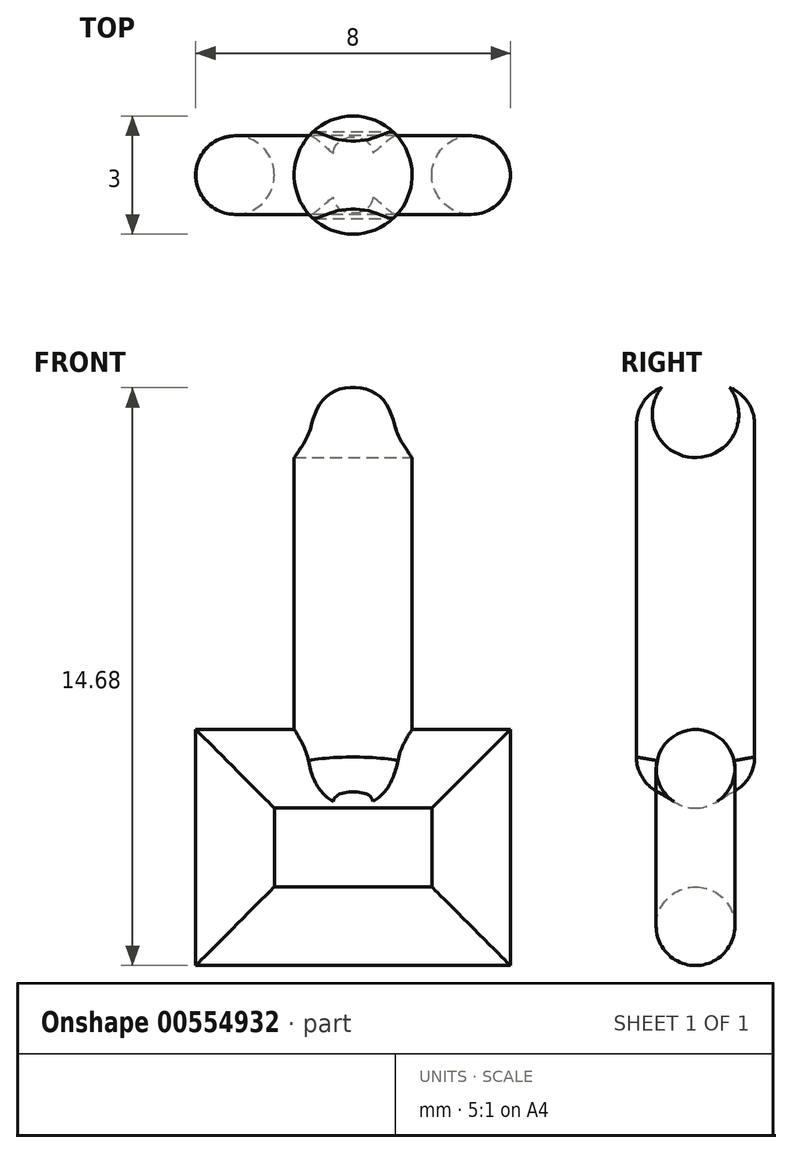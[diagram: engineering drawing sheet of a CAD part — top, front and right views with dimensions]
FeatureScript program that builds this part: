
annotation { "Feature Type Name" : "Feature", "Feature Type Description" : "" }
export const myFeature = defineFeature(function(context is Context, id is Id, definition is map)
    precondition{}
    {
        {
            var Q0;
            Q0=qCreatedBy(makeId("Front.planeOp"),FACE);
            var sketch = newSketch(context, id + "F0", { "sketchPlane" : qUnion([Q0])});
            skLineSegment(sketch, "E0.bottom", {"start": v(3, 4) * mm, "end": v(-3, 4) * mm});
            skLineSegment(sketch, "E0.top", {"start": v(3, 0) * mm, "end": v(-3, 0) * mm});
            skLineSegment(sketch, "E0.left", {"start": v(3, 4) * mm, "end": v(3, 0) * mm});
            skLineSegment(sketch, "E0.right", {"start": v(-3, 4) * mm, "end": v(-3, 0) * mm});
            skSolve(sketch);
        }
        {
            var Q0;
            Q0=qCreatedBy(makeId("Right.planeOp"),FACE);
            var sketch = newSketch(context, id + "F1", { "sketchPlane" : qUnion([Q0])});
            skPoint(sketch, "E1.0", {"position": v(0, 4) * mm});
            skPoint(sketch, "E2.0", {"position": v(0, 0) * mm});
            skPoint(sketch, "E3.0", {"position": v(0, 2) * mm});
            skCircle(sketch, "E4", {"center": v(0, 4) * mm, "radius": 1 * mm});
            skSolve(sketch);
        }
        {
            var Q0;
            Q0=makeQuery(id+"F1.imprint","IMPRINT",FACE,{"disambiguationData":[TD([[makeQuery(id+"F1.imprint","IMPRINT",EDGE,{"derivedFrom":sQuery(id+"F1.wireOp",EDGE,"E4")}),1.0]])]});
            var Q1;
            Q1=sQuery(id+"F0.wireOp",EDGE,"E0.bottom");
            var Q2;
            Q2=sQuery(id+"F0.wireOp",EDGE,"E0.left");
            var Q3;
            Q3=sQuery(id+"F0.wireOp",EDGE,"E0.right");
            var Q4;
            Q4=sQuery(id+"F0.wireOp",EDGE,"E0.top");
            sweep(context, id + "F2", {"profiles" : qUnion([Q0]), "path" : qUnion([Q1, Q2, Q3, Q4])});
        }
        {
            var Q0;
            Q0=qCreatedBy(makeId("Top.planeOp"),FACE);
            cPlane(context, id + "F3", {"entities" : qUnion([Q0]), "cplaneType" : CPlaneType.OFFSET, "offset" : 5 * mm, "width" : 150 * mm, "height" : 150 * mm});
        }
        {
            var Q0;
            Q0=qCreatedBy(id+"F3.planeOp",FACE);
            var sketch = newSketch(context, id + "F4", { "sketchPlane" : qUnion([Q0])});
            skCircle(sketch, "E5", {"center": v(0, 0) * mm, "radius": 1.5 * mm});
            skSolve(sketch);
        }
        {
            var Q0;
            Q0 = qSketchRegion(id + "F4", true);
            extrude(context, id + "F5", {"entities" : qUnion([Q0]), "operationType" : NewBodyOperationType.ADD, "oppositeDirection" : true, "depth" : 1 * mm, "offsetDistance" : 25 * mm});
        }
        {
            var Q0;
            Q0 = qSketchRegion(id + "F4", true);
            extrude(context, id + "F6", {"entities" : qUnion([Q0]), "operationType" : NewBodyOperationType.ADD, "depth" : 8 * mm, "offsetDistance" : 25 * mm});
        }
        {
            var Q0;
            Q0=qCreatedBy(makeId("Right.planeOp"),FACE);
            var sketch = newSketch(context, id + "F7", { "sketchPlane" : qUnion([Q0])});
            skLineSegment(sketch, "E6.0", {"start": v(-1.5, 13) * mm, "end": v(1.5, 13) * mm});
            skArc(sketch, "E7", {"start": v(-1.5, 13) * mm, "mid": v(0, 14.5) * mm, "end": v(1.5, 13) * mm});
            skLineSegment(sketch, "E8", {"start": v(0, 13) * mm, "end": v(0, 14.5) * mm});
            skSolve(sketch);
        }
        {
            var Q0;
            {var subQ3=sQuery(id+"F7.wireOp",EDGE,"E8");Q0=makeQuery(id+"F7.imprint","IMPRINT",FACE,{"disambiguationData":[TD([[makeQuery(id+"F7.imprint","IMPRINT",EDGE,{"derivedFrom":subQ3}),1.0]])]});}
            var Q1;
            Q1=sQuery(id+"F7.wireOp",EDGE,"E8");
            revolve(context, id + "F8", {"operationType" : NewBodyOperationType.ADD, "entities" : qUnion([Q0]), "axis" : qUnion([Q1]), "revolveType" : RevolveType.FULL});
        }
        {
            var Q0;
            Q0=qCreatedBy(makeId("Right.planeOp"),FACE);
            var sketch = newSketch(context, id + "F9", { "sketchPlane" : qUnion([Q0])});
            skArc(sketch, "E9", {"start": v(1.3, 13.75) * mm, "mid": v(0, 14.5) * mm, "end": v(-1.3, 13.75) * mm});
            skLineSegment(sketch, "E10.0", {"start": v(-1.1, 13) * mm, "end": v(1.1, 13) * mm});
            skCircle(sketch, "E11", {"center": v(0, 13) * mm, "radius": 1.1 * mm});
            skLineSegment(sketch, "E12", {"start": v(-1.3, 13.75) * mm, "end": v(1.3, 13.75) * mm});
            skPoint(sketch, "E13.orphan", {"position": v(1.5, 13) * mm});
            skPoint(sketch, "E14.orphan", {"position": v(-1.5, 13) * mm});
            skSolve(sketch);
        }
        {
            var Q0;
            Q0 = qSketchRegion(id + "F9", true);
            extrude(context, id + "F10", {"entities" : qUnion([Q0]), "operationType" : NewBodyOperationType.REMOVE, "endBound" : BoundingType.SYMMETRIC, "oppositeDirection" : true, "depth" : 25 * mm, "offsetDistance" : 25 * mm});
        }
        {
            var Q0;
            {var subQ0=sQuery(id+"F9.wireOp",EDGE,"E12");Q0=makeQuery(id+"F10.boolean.opBoolean","INTERSECT",EDGE,{"derivedFrom":[makeQuery(id+"F8.opRevolve","SWEPT_FACE",FACE,{"disambiguationData":[OSD([sQuery(id+"F7.wireOp",EDGE,"E7")])]}),makeQuery(id+"F10.opExtrude","SWEPT_FACE",FACE,{"disambiguationData":[OSD([subQ0]),TDD([makeQuery(id+"F9.imprint","IMPRINT",EDGE,{"disambiguationData":[TD([[makeQuery(id+"F9.imprint","INTERSECT",VERTEX,{"disambiguationData":[OD(1.0)],"derivedFrom":[sQuery(id+"F9.wireOp",EDGE,"E9"),subQ0]}),-1.0]])],"derivedFrom":subQ0})])]})]});}
            var Q1;
            {var subQ0=sQuery(id+"F9.wireOp",EDGE,"E12");Q1=makeQuery(id+"F10.boolean.opBoolean","INTERSECT",EDGE,{"derivedFrom":[makeQuery(id+"F8.opRevolve","SWEPT_FACE",FACE,{"disambiguationData":[OSD([sQuery(id+"F7.wireOp",EDGE,"E7")])]}),makeQuery(id+"F10.opExtrude","SWEPT_FACE",FACE,{"disambiguationData":[OSD([subQ0]),TDD([makeQuery(id+"F9.imprint","IMPRINT",EDGE,{"disambiguationData":[TD([[makeQuery(id+"F9.imprint","INTERSECT",VERTEX,{"disambiguationData":[OD(0.0)],"derivedFrom":[sQuery(id+"F9.wireOp",EDGE,"E9"),subQ0]}),1.0]])],"derivedFrom":subQ0})])]})]});}
            fillet(context, id + "F11", {"entities" : qUnion([Q0, Q1]), "radius" : 1 * mm, "tangentPropagation" : true, "allowEdgeOverflow" : false});
        }
        {
            var Q0;
            Q0=makeQuery(id+"F5.boolean.opBoolean","INTERSECT",EDGE,{"disambiguationData":[OD(0.0)],"derivedFrom":[makeQuery(id+"F2.opSweep","SWEPT_FACE",FACE,{"disambiguationData":[OSD([sQuery(id+"F0.wireOp",EDGE,"E0.bottom"),sQuery(id+"F1.wireOp",EDGE,"E4")])]}),makeQuery(id+"F5.opExtrude","CAP_FACE",FACE,{"disambiguationData":[OSD([sQuery(id+"F4.wireOp",EDGE,"E5")])],"isStart":false})]});
            var Q1;
            Q1=makeQuery(id+"F5.boolean.opBoolean","INTERSECT",EDGE,{"disambiguationData":[OD(1.0)],"derivedFrom":[makeQuery(id+"F2.opSweep","SWEPT_FACE",FACE,{"disambiguationData":[OSD([sQuery(id+"F0.wireOp",EDGE,"E0.bottom"),sQuery(id+"F1.wireOp",EDGE,"E4")])]}),makeQuery(id+"F5.opExtrude","CAP_FACE",FACE,{"disambiguationData":[OSD([sQuery(id+"F4.wireOp",EDGE,"E5")])],"isStart":false})]});
            fillet(context, id + "F12", {"entities" : qUnion([Q0, Q1]), "radius" : 5 * mm, "tangentPropagation" : true, "allowEdgeOverflow" : false});
        }
        {
            var Q0;
            {var subQ0=sQuery(id+"F4.wireOp",EDGE,"E5");var subQ1=makeQuery(id+"F5.opExtrude","SWEPT_FACE",FACE,{"disambiguationData":[OSD([subQ0])]});Q0=makeQuery(id+"F12.opFillet","BLEND_EDGE",EDGE,{"blendedFrom":[makeQuery(id+"F5.boolean.opBoolean","INTERSECT",EDGE,{"disambiguationData":[OD(0.0)],"derivedFrom":[makeQuery(id+"F2.opSweep","SWEPT_FACE",FACE,{"disambiguationData":[OSD([sQuery(id+"F0.wireOp",EDGE,"E0.bottom"),sQuery(id+"F1.wireOp",EDGE,"E4")])]}),makeQuery(id+"F5.opExtrude","CAP_FACE",FACE,{"disambiguationData":[OSD([subQ0])],"isStart":false})]}),makeQuery(id+"F6.boolean.opBoolean","MERGE",FACE,{"derivedFrom":[makeQuery(id+"F5.boolean.opBoolean","SPLIT",FACE,{"disambiguationData":[OD(0.0)],"derivedFrom":subQ1}),makeQuery(id+"F5.boolean.opBoolean","SPLIT",FACE,{"disambiguationData":[OD(1.0)],"derivedFrom":subQ1}),makeQuery(id+"F6.opExtrude","SWEPT_FACE",FACE,{"disambiguationData":[OSD([subQ0])]})]})],"blendedInto":[makeQuery(id+"F6.boolean.opBoolean","MERGE",FACE,{"derivedFrom":[makeQuery(id+"F5.boolean.opBoolean","SPLIT",FACE,{"disambiguationData":[OD(0.0)],"derivedFrom":subQ1}),makeQuery(id+"F5.boolean.opBoolean","SPLIT",FACE,{"disambiguationData":[OD(1.0)],"derivedFrom":subQ1}),makeQuery(id+"F6.opExtrude","SWEPT_FACE",FACE,{"disambiguationData":[OSD([subQ0])]})]})]});}
            var Q1;
            {var subQ0=sQuery(id+"F4.wireOp",EDGE,"E5");var subQ1=makeQuery(id+"F5.opExtrude","SWEPT_FACE",FACE,{"disambiguationData":[OSD([subQ0])]});Q1=makeQuery(id+"F12.opFillet","BLEND_EDGE",EDGE,{"blendedFrom":[makeQuery(id+"F5.boolean.opBoolean","INTERSECT",EDGE,{"disambiguationData":[OD(1.0)],"derivedFrom":[makeQuery(id+"F2.opSweep","SWEPT_FACE",FACE,{"disambiguationData":[OSD([sQuery(id+"F0.wireOp",EDGE,"E0.bottom"),sQuery(id+"F1.wireOp",EDGE,"E4")])]}),makeQuery(id+"F5.opExtrude","CAP_FACE",FACE,{"disambiguationData":[OSD([subQ0])],"isStart":false})]}),makeQuery(id+"F6.boolean.opBoolean","MERGE",FACE,{"derivedFrom":[makeQuery(id+"F5.boolean.opBoolean","SPLIT",FACE,{"disambiguationData":[OD(0.0)],"derivedFrom":subQ1}),makeQuery(id+"F5.boolean.opBoolean","SPLIT",FACE,{"disambiguationData":[OD(1.0)],"derivedFrom":subQ1}),makeQuery(id+"F6.opExtrude","SWEPT_FACE",FACE,{"disambiguationData":[OSD([subQ0])]})]})],"blendedInto":[makeQuery(id+"F6.boolean.opBoolean","MERGE",FACE,{"derivedFrom":[makeQuery(id+"F5.boolean.opBoolean","SPLIT",FACE,{"disambiguationData":[OD(0.0)],"derivedFrom":subQ1}),makeQuery(id+"F5.boolean.opBoolean","SPLIT",FACE,{"disambiguationData":[OD(1.0)],"derivedFrom":subQ1}),makeQuery(id+"F6.opExtrude","SWEPT_FACE",FACE,{"disambiguationData":[OSD([subQ0])]})]})]});}
            fillet(context, id + "F13", {"entities" : qUnion([Q0, Q1]), "radius" : 1 * mm, "tangentPropagation" : true, "allowEdgeOverflow" : false});
        }
    });
